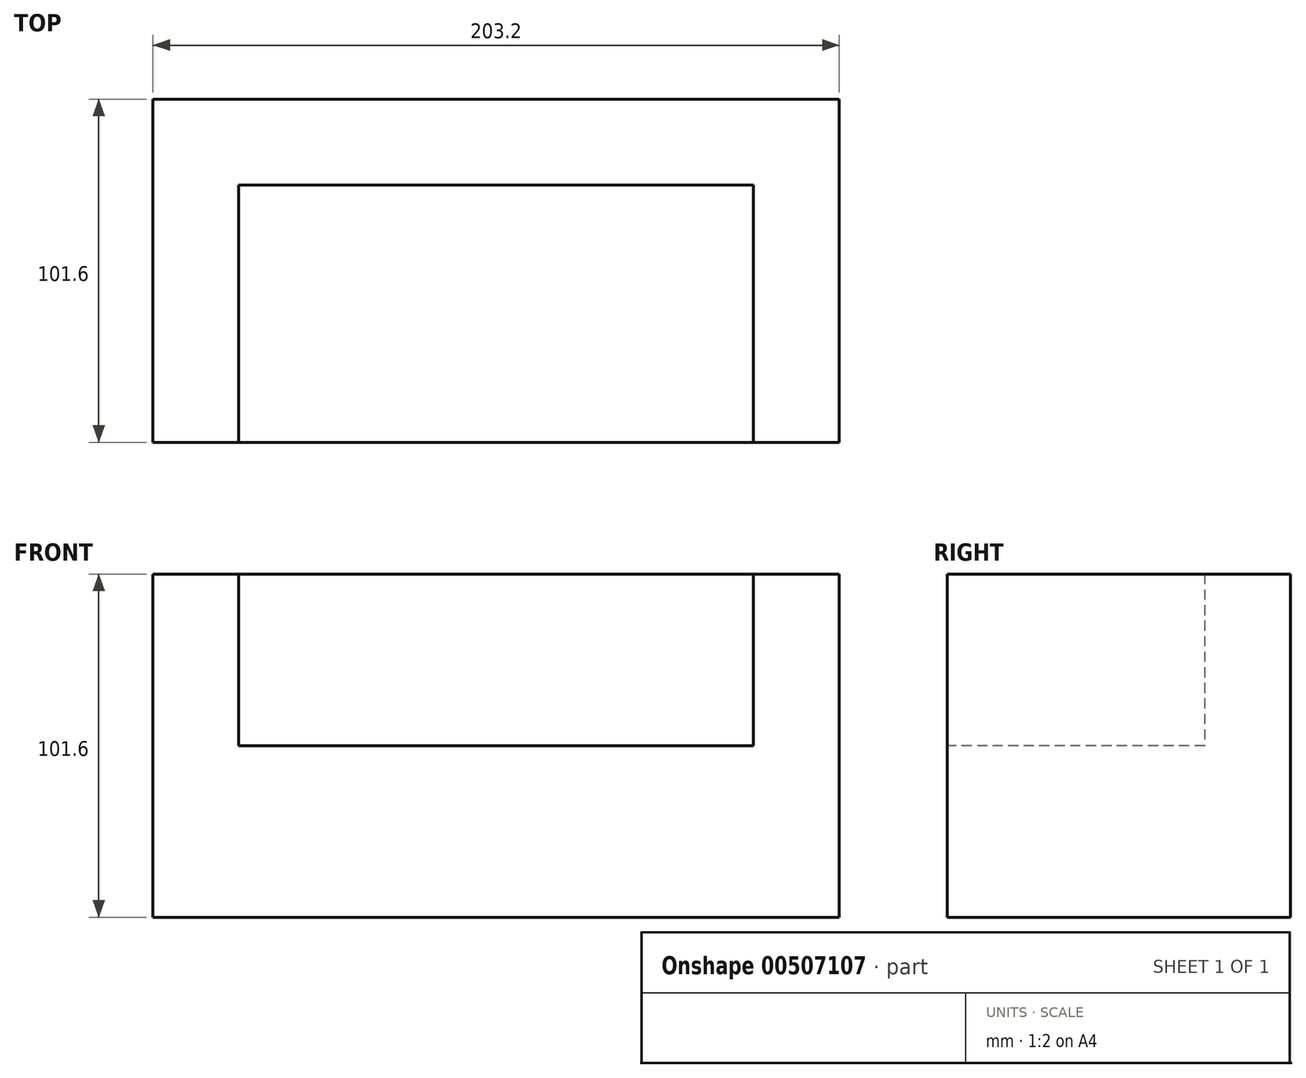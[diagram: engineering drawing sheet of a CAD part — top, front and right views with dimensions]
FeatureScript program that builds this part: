
annotation { "Feature Type Name" : "Feature", "Feature Type Description" : "" }
export const myFeature = defineFeature(function(context is Context, id is Id, definition is map)
    precondition{}
    {
        {
            var Q0;
            Q0=qCreatedBy(makeId("Front.planeOp"),FACE);
            var sketch = newSketch(context, id + "F0", { "sketchPlane" : qUnion([Q0])});
            skLineSegment(sketch, "E0", {"start": v(0, 0) * mm, "end": v(-203.2, 0) * mm});
            skLineSegment(sketch, "E1", {"start": v(-203.2, 0) * mm, "end": v(-203.2, 101.6) * mm});
            skLineSegment(sketch, "E2", {"start": v(-203.2, 101.6) * mm, "end": v(0, 101.6) * mm});
            skLineSegment(sketch, "E3", {"start": v(0, 101.6) * mm, "end": v(0, 0) * mm});
            skSolve(sketch);
        }
        {
            var Q0;
            Q0=makeQuery(id+"F0.imprint","IMPRINT",FACE,{"disambiguationData":[TD([[makeQuery(id+"F0.imprint","IMPRINT",EDGE,{"derivedFrom":sQuery(id+"F0.wireOp",EDGE,"E0")}),-1.0]])]});
            extrude(context, id + "F1", {"entities" : qUnion([Q0]), "oppositeDirection" : true, "depth" : 101.6 * mm});
        }
        {
            var Q0;
            Q0=makeQuery(id+"F1.opExtrude","CAP_FACE",FACE,{"disambiguationData":[OSD([sQuery(id+"F0.wireOp",EDGE,"E0"),sQuery(id+"F0.wireOp",EDGE,"E1"),sQuery(id+"F0.wireOp",EDGE,"E2"),sQuery(id+"F0.wireOp",EDGE,"E3")])],"isStart":true});
            var sketch = newSketch(context, id + "F2", { "sketchPlane" : qUnion([Q0])});
            skLineSegment(sketch, "E4", {"start": v(-177.8, 101.6) * mm, "end": v(-177.8, 50.8) * mm});
            skLineSegment(sketch, "E5", {"start": v(-177.8, 50.8) * mm, "end": v(-25.4, 50.8) * mm});
            skLineSegment(sketch, "E6", {"start": v(-25.4, 50.8) * mm, "end": v(-25.4, 101.6) * mm});
            skLineSegment(sketch, "E7", {"start": v(-25.4, 101.6) * mm, "end": v(-177.8, 101.6) * mm});
            skSolve(sketch);
        }
        {
            var Q0;
            Q0=makeQuery(id+"F2.imprint","IMPRINT",FACE,{"disambiguationData":[TD([[makeQuery(id+"F2.imprint","IMPRINT",EDGE,{"derivedFrom":sQuery(id+"F2.wireOp",EDGE,"E4")}),1.0]])]});
            extrude(context, id + "F3", {"entities" : qUnion([Q0]), "operationType" : NewBodyOperationType.REMOVE, "oppositeDirection" : true, "depth" : 76.2 * mm});
        }
    });
